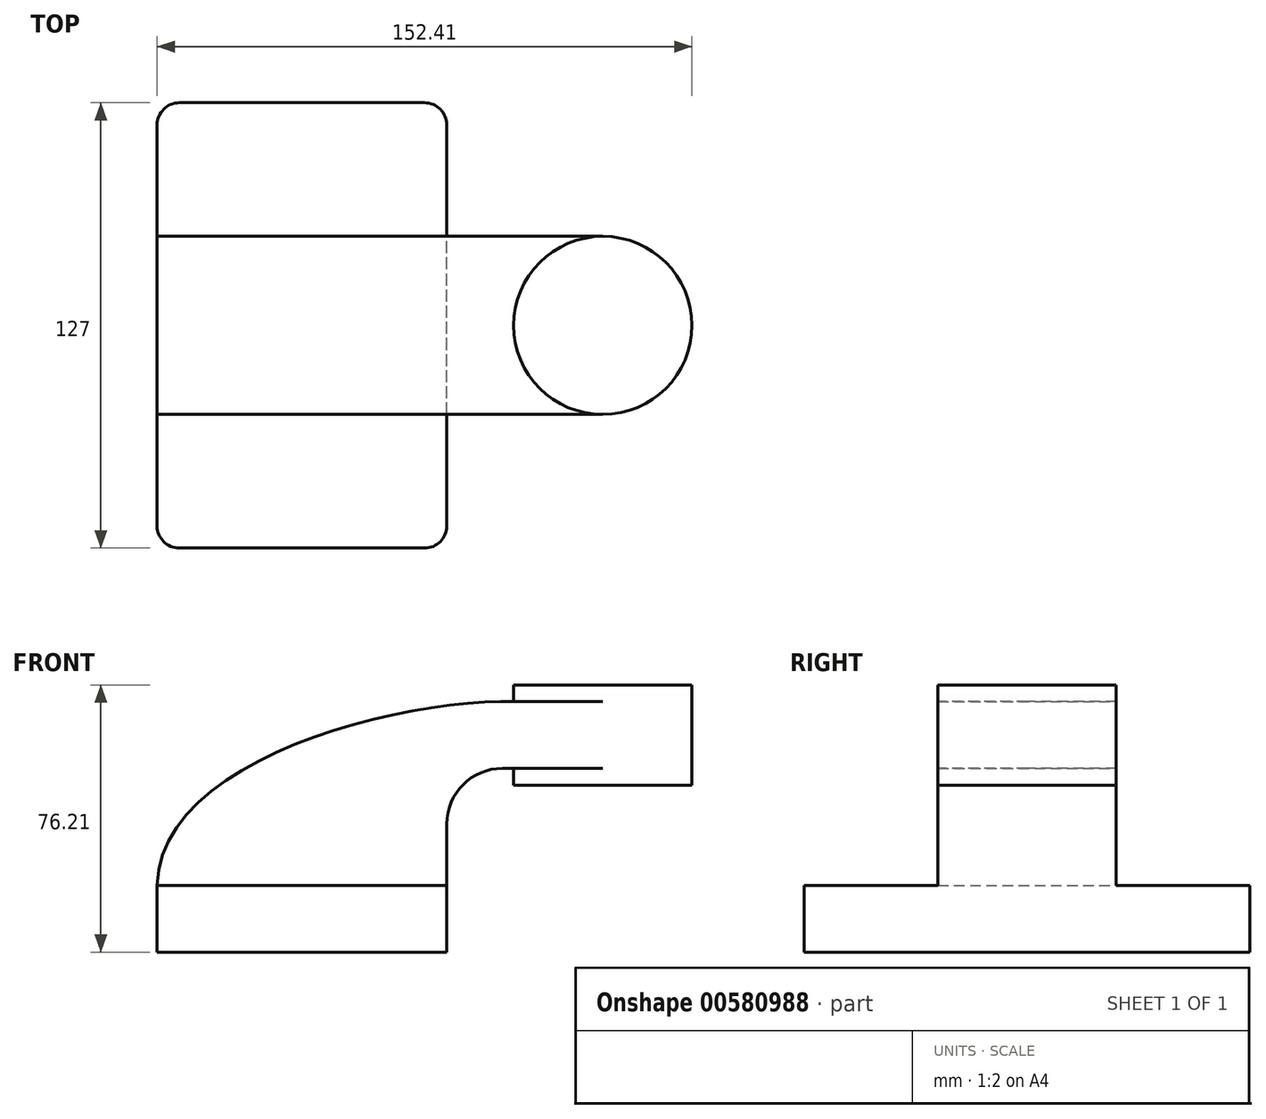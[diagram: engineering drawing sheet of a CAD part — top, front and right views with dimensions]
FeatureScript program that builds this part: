
annotation { "Feature Type Name" : "Feature", "Feature Type Description" : "" }
export const myFeature = defineFeature(function(context is Context, id is Id, definition is map)
    precondition{}
    {
        {
            var Q0;
            Q0=qCreatedBy(makeId("Front.planeOp"),FACE);
            var sketch = newSketch(context, id + "F0", { "sketchPlane" : qUnion([Q0])});
            skLineSegment(sketch, "E0.bottom", {"start": v(41.27, 9.53) * mm, "end": v(-41.28, 9.53) * mm});
            skLineSegment(sketch, "E0.top", {"start": v(41.28, -9.52) * mm, "end": v(-41.27, -9.52) * mm});
            skLineSegment(sketch, "E0.left", {"start": v(41.28, 9.53) * mm, "end": v(41.28, -9.52) * mm});
            skLineSegment(sketch, "E0.right", {"start": v(-41.28, 9.53) * mm, "end": v(-41.28, -9.52) * mm});
            skPoint(sketch, "E0.middle", {"position": v(0, 0) * mm});
            skLineSegment(sketch, "E1.bottom", {"start": v(111.13, 66.68) * mm, "end": v(60.33, 66.68) * mm});
            skLineSegment(sketch, "E1.top", {"start": v(111.13, 38.1) * mm, "end": v(60.33, 38.1) * mm});
            skLineSegment(sketch, "E1.left", {"start": v(111.13, 66.68) * mm, "end": v(111.13, 38.1) * mm});
            skLineSegment(sketch, "E1.right", {"start": v(60.33, 66.68) * mm, "end": v(60.33, 38.1) * mm});
            skPoint(sketch, "E1.middle", {"position": v(85.72, 52.39) * mm});
            skLineSegment(sketch, "E2", {"start": v(41.27, 9.53) * mm, "end": v(41.27, 27) * mm});
            skArc(sketch, "E3", {"start": v(41.27, 27) * mm, "mid": v(45.92, 38.23) * mm, "end": v(57.15, 42.88) * mm});
            skLineSegment(sketch, "E4", {"start": v(57.15, 42.88) * mm, "end": v(85.72, 42.88) * mm});
            skLineSegment(sketch, "E5.0", {"start": v(57.15, 61.93) * mm, "end": v(85.72, 61.93) * mm});
            skArc(sketch, "E5.1", {"start": v(22.22, 27) * mm, "mid": v(32.45, 51.7) * mm, "end": v(57.15, 61.93) * mm});
            skLineSegment(sketch, "E5.2", {"start": v(22.22, 9.53) * mm, "end": v(22.22, 27) * mm});
            skLineSegment(sketch, "E6", {"start": v(85.73, 38.1) * mm, "end": v(85.73, 66.68) * mm});
            skFitSpline(sketch, "E7", {"points": [v(-41.28, 9.52) * mm, v(57.15, 61.93) * mm], "startDerivative": vector(1.65, 104.4) * mm, "endDerivative": vector(99.76, 0.53) * mm});
            skSolve(sketch);
        }
        {
            var Q0;
            Q0=makeQuery(id+"F0.imprint","IMPRINT",FACE,{"disambiguationData":[TD([[makeQuery(id+"F0.imprint","IMPRINT",EDGE,{"derivedFrom":sQuery(id+"F0.wireOp",EDGE,"E0.top")}),-1.0]])]});
            extrude(context, id + "F1", {"entities" : qUnion([Q0]), "endBound" : BoundingType.SYMMETRIC, "depth" : 127 * mm, "offsetDistance" : 25.4 * mm});
        }
        {
            var Q0;
            {var subQ0=sQuery(id+"F0.wireOp",EDGE,"E7");var subQ1=sQuery(id+"F0.wireOp",EDGE,"E5.1");var subQ3=makeQuery(id+"F0.imprint","INTERSECT",VERTEX,{"derivedFrom":[subQ1,subQ0]});Q0=makeQuery(id+"F0.imprint","IMPRINT",FACE,{"disambiguationData":[TD([[makeQuery(id+"F0.imprint","IMPRINT",EDGE,{"disambiguationData":[TD([[subQ3,-1.0]])],"derivedFrom":subQ1}),-1.0]])]});}
            var Q1;
            Q1=makeQuery(id+"F0.imprint","IMPRINT",FACE,{"disambiguationData":[TD([[makeQuery(id+"F0.imprint","IMPRINT",EDGE,{"derivedFrom":sQuery(id+"F0.wireOp",EDGE,"E0.top")}),-1.0]])]});
            var Q2;
            {var subQ1=sQuery(id+"F0.wireOp",EDGE,"E2");Q2=makeQuery(id+"F0.imprint","IMPRINT",FACE,{"disambiguationData":[TD([[makeQuery(id+"F0.imprint","IMPRINT",EDGE,{"derivedFrom":subQ1}),1.0]])]});}
            var Q3;
            {var subQ0=sQuery(id+"F0.wireOp",EDGE,"E5.0");var subQ1=sQuery(id+"F0.wireOp",EDGE,"E1.right");var subQ2=makeQuery(id+"F0.imprint","INTERSECT",VERTEX,{"derivedFrom":[subQ1,subQ0]});Q3=makeQuery(id+"F0.imprint","IMPRINT",FACE,{"disambiguationData":[TD([[makeQuery(id+"F0.imprint","IMPRINT",EDGE,{"disambiguationData":[TD([[subQ2,-1.0]])],"derivedFrom":subQ1}),1.0]])]});}
            extrude(context, id + "F2", {"entities" : qUnion([Q0, Q1, Q2, Q3]), "operationType" : NewBodyOperationType.ADD, "endBound" : BoundingType.SYMMETRIC, "depth" : 50.8 * mm, "offsetDistance" : 25.4 * mm});
        }
        {
            var Q0;
            {var subQ3=sQuery(id+"F0.wireOp",EDGE,"E5.2");Q0=makeQuery(id+"F0.imprint","IMPRINT",FACE,{"disambiguationData":[TD([[makeQuery(id+"F0.imprint","IMPRINT",EDGE,{"derivedFrom":subQ3}),1.0]])]});}
            extrude(context, id + "F3", {"entities" : qUnion([Q0]), "operationType" : NewBodyOperationType.ADD, "endBound" : BoundingType.SYMMETRIC, "depth" : 15.88 * mm, "offsetDistance" : 25.4 * mm});
        }
        {
            var Q0;
            {var subQ0=sQuery(id+"F0.wireOp",EDGE,"E1.left");Q0=makeQuery(id+"F0.imprint","IMPRINT",FACE,{"disambiguationData":[TD([[makeQuery(id+"F0.imprint","IMPRINT",EDGE,{"derivedFrom":subQ0}),-1.0]])]});}
            var Q1;
            Q1=sQuery(id+"F0.wireOp",EDGE,"E6");
            revolve(context, id + "F4", {"operationType" : NewBodyOperationType.ADD, "entities" : qUnion([Q0]), "axis" : qUnion([Q1]), "revolveType" : RevolveType.FULL});
        }
        {
            var Q0;
            Q0=makeQuery(id+"F1.opExtrude","CAP_EDGE",EDGE,{"disambiguationData":[OSD([sQuery(id+"F0.wireOp",EDGE,"E0.right")])],"isStart":false});
            var Q1;
            Q1=makeQuery(id+"F1.opExtrude","CAP_EDGE",EDGE,{"disambiguationData":[OSD([sQuery(id+"F0.wireOp",EDGE,"E0.left")])],"isStart":false});
            var Q2;
            Q2=makeQuery(id+"F1.opExtrude","CAP_EDGE",EDGE,{"disambiguationData":[OSD([sQuery(id+"F0.wireOp",EDGE,"E0.left")])],"isStart":true});
            var Q3;
            Q3=makeQuery(id+"F1.opExtrude","CAP_EDGE",EDGE,{"disambiguationData":[OSD([sQuery(id+"F0.wireOp",EDGE,"E0.right")])],"isStart":true});
            fillet(context, id + "F5", {"entities" : qUnion([Q0, Q1, Q2, Q3]), "radius" : 6.35 * mm, "tangentPropagation" : true, "allowEdgeOverflow" : false});
        }
    });
